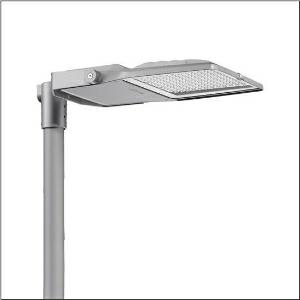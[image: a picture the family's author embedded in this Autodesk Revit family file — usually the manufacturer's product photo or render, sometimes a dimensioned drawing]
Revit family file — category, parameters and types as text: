
# Revit family: floodlight_fl_21_midi___pl64_5xa7786f2e3a_6eef
name_source: partatom
category: Lighting Fixtures
units: mm (PartAtom-declared; Revit-internal decimal feet)

## family parameters
Cut with Voids When Loaded = No
Host = Face
Light Source = No
Part Type = Normal
Room Calculation Point = No
Round Connector Dimension = Use Diameter
Shared = No

## types (1)
- --- (1 x LED, 34530 lm, 271.6 W, 3000K)
    Apparent Load = 272 VA
    CIE Flux Codes = 28 80 98 100 100
    Color Rendering = 70
    Color Temperature = 3000K
    Default Elevation = 1800 mm
    Description = Floodlight FL 21 midi, floodlight, primary light control with lens, of PMMA, primary optical cover: protective disc, of toughened safety glass, transparent, light distribution: PL64, light emission: direct distribution, installation type: surface-mounted, LED, High Power LED, rated luminous flux: 34.530lm, luminous efficacy: 127lm/W, light colour: 730, colour temperature: 3000K, control gear: Smart Interface (Zhaga), control: flexible luminous flux parameterisation, time-dependent luminous flux control, constant luminous flux control, overheat protection, pre-setting: logarithmic dimming characteristic, with terminal, 6-pole, mains connection: 220..240V, AC, 50/60Hz, start of lifetime: 272W, end of service life: 287W, reduction: 123W, luminaire housing, of diecast aluminium, powder-coated, Siteco® metallic grey (DB 702S), corrosivity category C5 mid according to DIN EN ISO 12944, suitable for swimming pools, chlorine-resistant, sealing non-destructively replaceable, please order mast flange separately, mast bracket, of steel, galvanised, powder-coated, Siteco® metallic grey (DB 702S), Smart Interface below and above, protection rating (complete): IP66, insulation class (complete): insulation class II (safety insulation), certification: CE, ENEC, VDE, protection symbol: D, impact resistance: IK08, permissible operating ambient temperature: -40..+40°C, permissible operating ambient temperature for outdoor applications: -40..+50°C, standard: DIN EN 12944, LABS conformity tested according to VDMA 24364:2018-05, packaging unit: 1 piece

Light Distribution: PL64
    Height = 76 mm
    Lamp = 1 x LED
    Lamp Light Flux = 34530 lm
    Lamp Power = 271.6 W
    Lamp count = 1
    Length = 657 mm
    Luminous efficacy = 127 lm/W
    Manufacturer = Siteco
    ModVariant = No
    Model = 5XA7786F2E3A
    Number of Poles = 1
    OnlyDefault = Yes
    Power Factor = 1
    Product Name = Floodlight FL 21 midi | PL64
    Product group = floodlight | pylon annexe
    ProductGroupID = 6200
    Protection Class = Protection class II
    Protection Degree = IP 66
    RLX_Detail_Level = 1
    RLX_Emergency_Light_Flux = 0 lm
    RLX_Emergency_Type = 0
    RLX_Emergency_Type_DB = No
    RlxData = <blob elided: 153613 chars, md5=02af938f>
    Socket = socket
    Standby Power = 0 W
    System Light Flux = 34530 lm
    System Power = 272 W
    Type Comments = factory setting: luminous flux: 100 % | dim-lin: 254 | 620 mA
    Type Image = l_1007123.jpg
    URL = http://relux.com
    VarID = @adj_180166
    Voltage = 0 V
    Weight = 0.00 kg
    Width = 442 mm

## geometry (parser evidence)
native form markers: Blend x4, Sweep x14
no freeform markers — native parametric forms only
